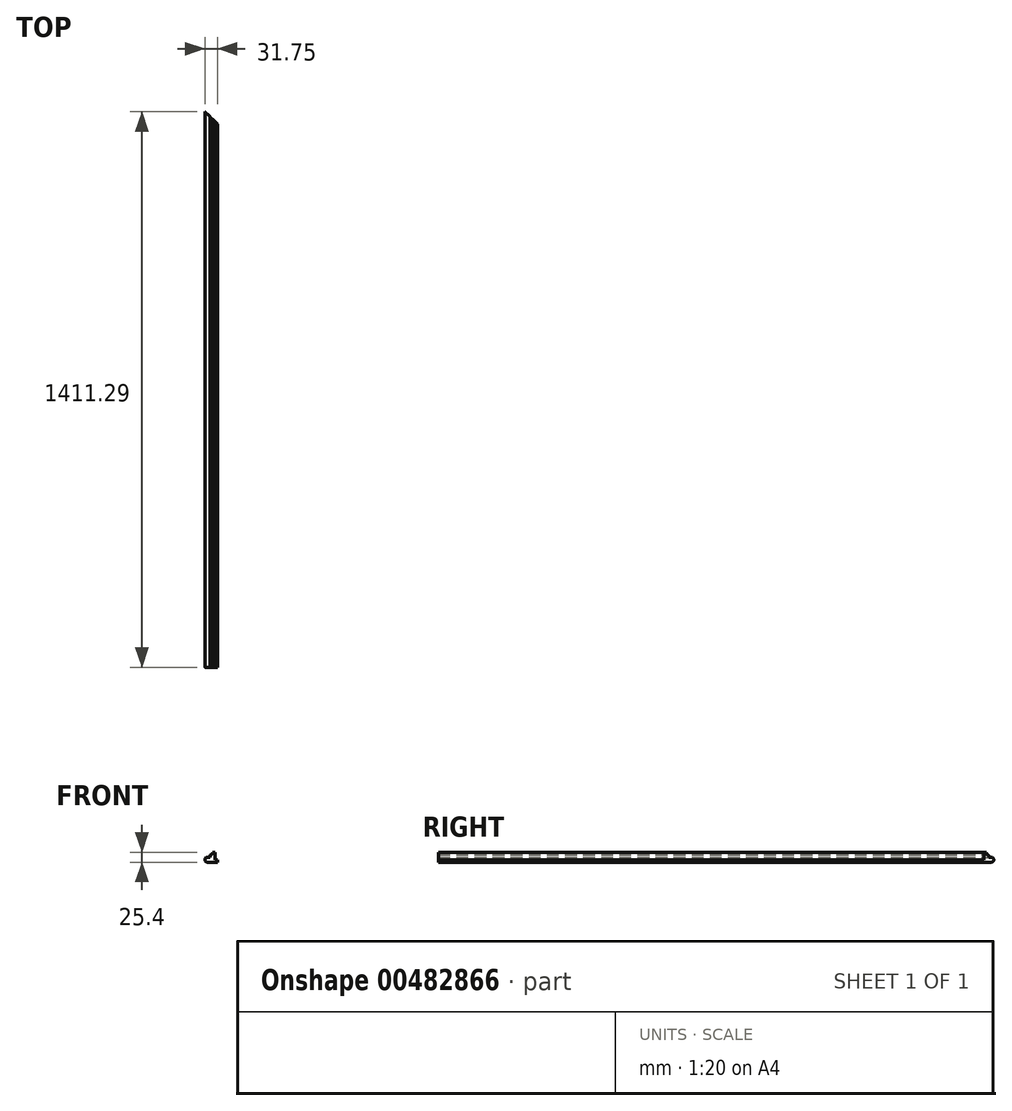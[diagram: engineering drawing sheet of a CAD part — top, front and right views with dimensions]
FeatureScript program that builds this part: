
annotation { "Feature Type Name" : "Feature", "Feature Type Description" : "" }
export const myFeature = defineFeature(function(context is Context, id is Id, definition is map)
    precondition{}
    {
        {
            var Q0;
            Q0=qCreatedBy(makeId("Front.planeOp"),FACE);
            var sketch = newSketch(context, id + "F0", { "sketchPlane" : qUnion([Q0])});
            skLineSegment(sketch, "E0", {"start": v(-6.35, 25.4) * mm, "end": v(-6.35, 6.35) * mm});
            skLineSegment(sketch, "E1", {"start": v(-6.35, 6.35) * mm, "end": v(0, 6.35) * mm});
            skLineSegment(sketch, "E2", {"start": v(0, 6.35) * mm, "end": v(0, 0) * mm});
            skLineSegment(sketch, "E3", {"start": v(0, 0) * mm, "end": v(-31.75, 0) * mm});
            skLineSegment(sketch, "E4", {"start": v(-6.35, 25.4) * mm, "end": v(-12.7, 25.4) * mm});
            skLineSegment(sketch, "E5", {"start": v(-12.7, 25.4) * mm, "end": v(-12.7, 19.05) * mm});
            skLineSegment(sketch, "E6", {"start": v(-12.7, 19.05) * mm, "end": v(-19.05, 19.05) * mm});
            skLineSegment(sketch, "E7", {"start": v(-19.05, 19.05) * mm, "end": v(-19.05, 12.7) * mm});
            skLineSegment(sketch, "E8", {"start": v(-19.05, 12.7) * mm, "end": v(-31.75, 12.7) * mm});
            skLineSegment(sketch, "E9", {"start": v(-31.75, 12.7) * mm, "end": v(-31.75, 0) * mm});
            skSolve(sketch);
        }
        {
            var Q0;
            Q0=makeQuery(id+"F0.imprint","IMPRINT",FACE,{"disambiguationData":[TD([[makeQuery(id+"F0.imprint","IMPRINT",EDGE,{"derivedFrom":sQuery(id+"F0.wireOp",EDGE,"E0")}),-1.0]])]});
            extrude(context, id + "F1", {"entities" : qUnion([Q0]), "depth" : 1447.8 * mm});
        }
        {
            var Q0;
            Q0=makeQuery(id+"F1.opExtrude","SWEPT_EDGE",EDGE,{"disambiguationData":[OSD([sQuery(id+"F0.wireOp",EDGE,"E5"),sQuery(id+"F0.wireOp",EDGE,"E6")])]});
            var Q1;
            Q1=makeQuery(id+"F1.opExtrude","SWEPT_EDGE",EDGE,{"disambiguationData":[OSD([sQuery(id+"F0.wireOp",EDGE,"E6"),sQuery(id+"F0.wireOp",EDGE,"E7")])]});
            fillet(context, id + "F2", {"entities" : qUnion([Q0, Q1]), "radius" : 3.17 * mm, "tangentPropagation" : true, "allowEdgeOverflow" : false});
        }
        {
            var Q0;
            Q0=makeQuery(id+"F1.opExtrude","SWEPT_EDGE",EDGE,{"disambiguationData":[OSD([sQuery(id+"F0.wireOp",EDGE,"E8"),sQuery(id+"F0.wireOp",EDGE,"E9")])]});
            var Q1;
            Q1=makeQuery(id+"F1.opExtrude","SWEPT_EDGE",EDGE,{"disambiguationData":[OSD([sQuery(id+"F0.wireOp",EDGE,"E3"),sQuery(id+"F0.wireOp",EDGE,"E9")])]});
            fillet(context, id + "F3", {"entities" : qUnion([Q0, Q1]), "radius" : 6.35 * mm, "tangentPropagation" : true, "allowEdgeOverflow" : false});
        }
        {
            var Q0;
            Q0=makeQuery(id+"F1.opExtrude","SWEPT_FACE",FACE,{"disambiguationData":[OSD([sQuery(id+"F0.wireOp",EDGE,"E1")])]});
            var sketch = newSketch(context, id + "F4", { "sketchPlane" : qUnion([Q0])});
            skLineSegment(sketch, "E10", {"start": v(0, -68.26) * mm, "end": v(-49.27, -19) * mm});
            skLineSegment(sketch, "E11", {"start": v(-49.27, -19) * mm, "end": v(-49.27, 0) * mm});
            skLineSegment(sketch, "E12", {"start": v(-49.27, 0) * mm, "end": v(0, 0) * mm});
            skLineSegment(sketch, "E13", {"start": v(0, 0) * mm, "end": v(0, -68.26) * mm});
            skLineSegment(sketch, "E14", {"start": v(-6.35, -61.91) * mm, "end": v(0, -61.91) * mm, "construction": true});
            skSolve(sketch);
        }
        {
            var Q0;
            Q0 = qSketchRegion(id + "F4", true);
            extrude(context, id + "F5", {"entities" : qUnion([Q0]), "operationType" : NewBodyOperationType.REMOVE, "endBound" : BoundingType.SYMMETRIC, "oppositeDirection" : true, "depth" : 116.84 * mm});
        }
    });
